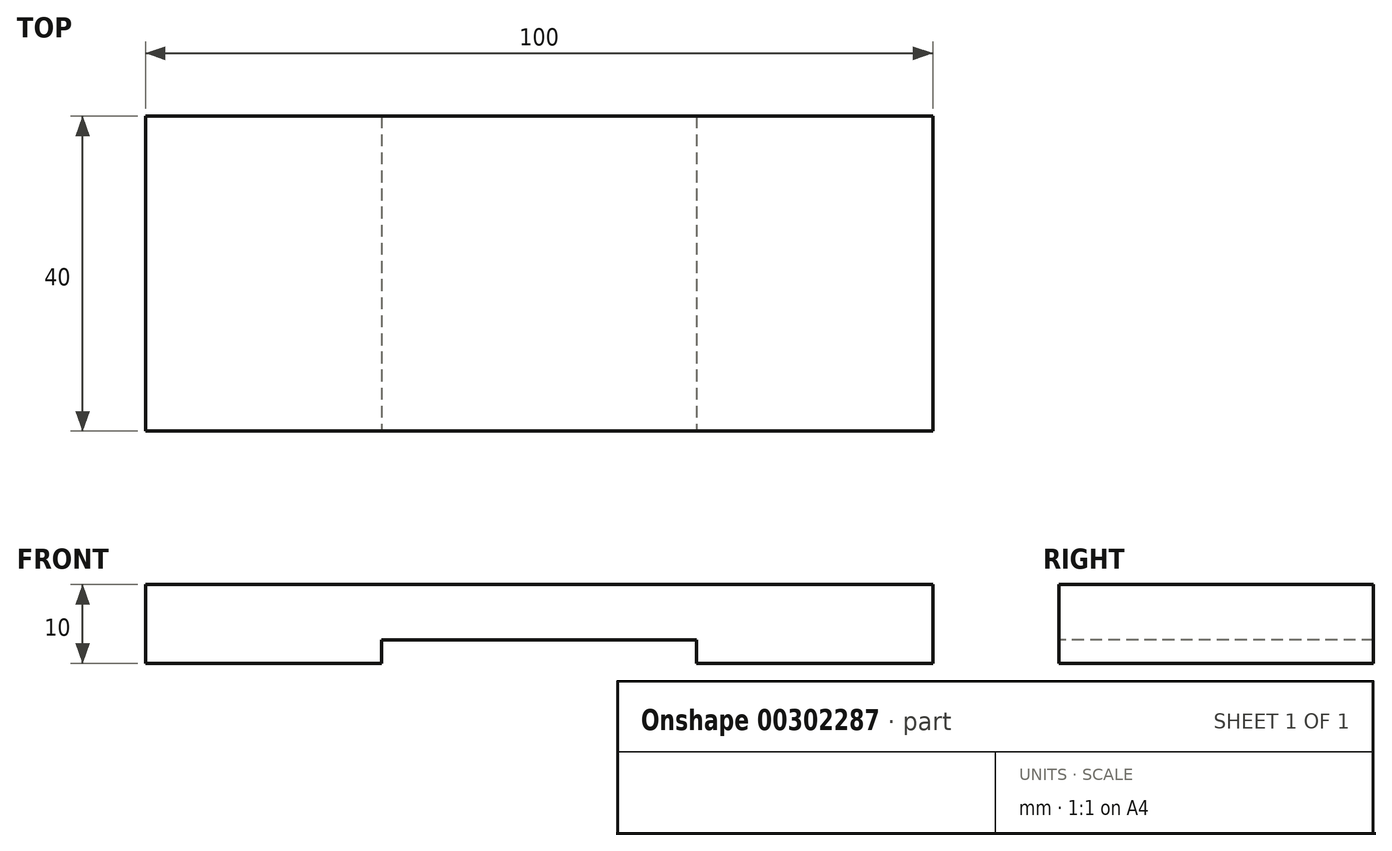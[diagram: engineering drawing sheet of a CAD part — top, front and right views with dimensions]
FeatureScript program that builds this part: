
annotation { "Feature Type Name" : "Feature", "Feature Type Description" : "" }
export const myFeature = defineFeature(function(context is Context, id is Id, definition is map)
    precondition{}
    {
        {
            var Q0;
            Q0=qCreatedBy(makeId("Top.planeOp"),FACE);
            var sketch = newSketch(context, id + "F0", { "sketchPlane" : qUnion([Q0])});
            skLineSegment(sketch, "E0.bottom", {"start": v(0, 0) * mm, "end": v(-100, 0) * mm});
            skLineSegment(sketch, "E0.top", {"start": v(0, 40) * mm, "end": v(-100, 40) * mm});
            skLineSegment(sketch, "E0.left", {"start": v(0, 0) * mm, "end": v(0, 40) * mm});
            skLineSegment(sketch, "E0.right", {"start": v(-100, 0) * mm, "end": v(-100, 40) * mm});
            skSolve(sketch);
        }
        {
            var Q0;
            Q0=makeQuery(id+"F0.imprint","IMPRINT",FACE,{"disambiguationData":[TD([[makeQuery(id+"F0.imprint","IMPRINT",EDGE,{"derivedFrom":sQuery(id+"F0.wireOp",EDGE,"E0.bottom")}),-1.0]])]});
            extrude(context, id + "F1", {"entities" : qUnion([Q0]), "depth" : 10 * mm});
        }
        {
            var Q0;
            Q0=makeQuery(id+"F1.opExtrude","SWEPT_FACE",FACE,{"disambiguationData":[OSD([sQuery(id+"F0.wireOp",EDGE,"E0.bottom")])]});
            var sketch = newSketch(context, id + "F2", { "sketchPlane" : qUnion([Q0])});
            skLineSegment(sketch, "E1", {"start": v(-70, 0) * mm, "end": v(-70, 35) * mm});
            skArc(sketch, "E2", {"start": v(-70, 35) * mm, "mid": v(-50, 55) * mm, "end": v(-30, 35) * mm});
            skLineSegment(sketch, "E3", {"start": v(-30, 35) * mm, "end": v(-30, 0) * mm});
            skLineSegment(sketch, "E4", {"start": v(-70, 0) * mm, "end": v(-30, 0) * mm});
            skSolve(sketch);
        }
        {
            var Q0;
            {var subQ0=sQuery(id+"F2.wireOp",EDGE,"E2");Q0=makeQuery(id+"F2.imprint","IMPRINT",FACE,{"disambiguationData":[TD([[makeQuery(id+"F2.imprint","IMPRINT",EDGE,{"derivedFrom":subQ0}),-1.0]])]});}
            var Q1;
            {var subQ0=sQuery(id+"F2.wireOp",EDGE,"E1");var subQ1=sQuery(id+"F0.wireOp",EDGE,"E0.bottom");var subQ2=makeQuery(id+"F1.opExtrude","CAP_EDGE",EDGE,{"disambiguationData":[OSD([subQ1])],"isStart":true});var subQ3=makeQuery(id+"F2.imprint","INTERSECT",VERTEX,{"derivedFrom":[subQ2,subQ0]});Q1=makeQuery(id+"F2.imprint","IMPRINT",FACE,{"disambiguationData":[TD([[makeQuery(id+"F2.imprint","IMPRINT",EDGE,{"disambiguationData":[TD([[subQ3,-1.0]])],"derivedFrom":subQ0}),-1.0]])]});}
            extrude(context, id + "F3", {"entities" : qUnion([Q0, Q1]), "operationType" : NewBodyOperationType.ADD, "oppositeDirection" : true, "depth" : 10 * mm});
        }
        {
            var Q0;
            Q0=makeQuery(id+"F3.boolean.opBoolean","MERGE",FACE,{"derivedFrom":[makeQuery(id+"F1.opExtrude","SWEPT_FACE",FACE,{"disambiguationData":[OSD([sQuery(id+"F0.wireOp",EDGE,"E0.bottom")])]}),makeQuery(id+"F3.opExtrude","CAP_FACE",FACE,{"disambiguationData":[OSD([sQuery(id+"F2.wireOp",EDGE,"E1"),sQuery(id+"F2.wireOp",EDGE,"E2"),sQuery(id+"F2.wireOp",EDGE,"E3"),sQuery(id+"F2.wireOp",EDGE,"E4")])],"isStart":true})]});
            var sketch = newSketch(context, id + "F4", { "sketchPlane" : qUnion([Q0])});
            skLineSegment(sketch, "E5.bottom", {"start": v(-70, 0) * mm, "end": v(-30, 0) * mm});
            skLineSegment(sketch, "E5.top", {"start": v(-70, 3) * mm, "end": v(-30, 3) * mm});
            skLineSegment(sketch, "E5.left", {"start": v(-70, 0) * mm, "end": v(-70, 3) * mm});
            skLineSegment(sketch, "E5.right", {"start": v(-30, 0) * mm, "end": v(-30, 3) * mm});
            skSolve(sketch);
        }
        {
            var Q0;
            Q0=makeQuery(id+"F4.imprint","IMPRINT",FACE,{"disambiguationData":[TD([[makeQuery(id+"F4.imprint","IMPRINT",EDGE,{"derivedFrom":sQuery(id+"F4.wireOp",EDGE,"E5.bottom")}),-1.0]])]});
            extrude(context, id + "F5", {"entities" : qUnion([Q0]), "operationType" : NewBodyOperationType.REMOVE, "endBound" : BoundingType.THROUGH_ALL, "oppositeDirection" : true, "depth" : 25 * mm});
        }
        {
            var Q0;
            Q0=makeQuery(id+"F3.boolean.opBoolean","MERGE",FACE,{"derivedFrom":[makeQuery(id+"F1.opExtrude","SWEPT_FACE",FACE,{"disambiguationData":[OSD([sQuery(id+"F0.wireOp",EDGE,"E0.bottom")])]}),makeQuery(id+"F3.opExtrude","CAP_FACE",FACE,{"disambiguationData":[OSD([sQuery(id+"F2.wireOp",EDGE,"E1"),sQuery(id+"F2.wireOp",EDGE,"E2"),sQuery(id+"F2.wireOp",EDGE,"E3"),sQuery(id+"F2.wireOp",EDGE,"E4")])],"isStart":true})]});
            var sketch = newSketch(context, id + "F6", { "sketchPlane" : qUnion([Q0])});
            skCircle(sketch, "E6", {"center": v(-50, 35) * mm, "radius": 2.25 * mm});
            skSolve(sketch);
        }
        {
            var Q0;
            Q0 = qSketchRegion(id + "F6", true);
            extrude(context, id + "F7", {"entities" : qUnion([Q0]), "operationType" : NewBodyOperationType.REMOVE, "endBound" : BoundingType.THROUGH_ALL, "oppositeDirection" : true, "depth" : 25 * mm});
        }
    });
